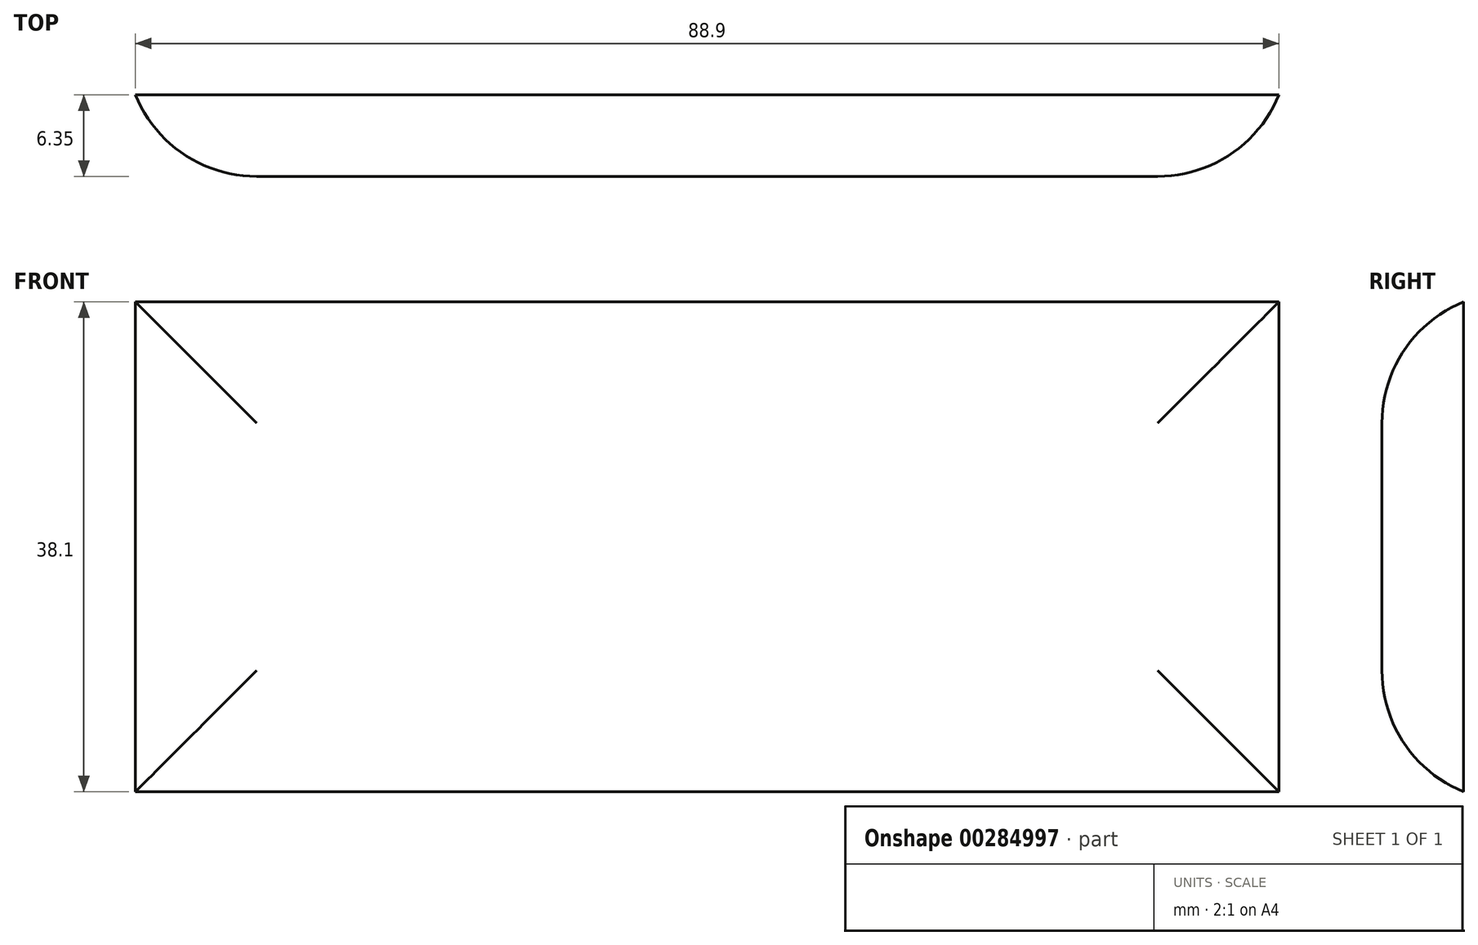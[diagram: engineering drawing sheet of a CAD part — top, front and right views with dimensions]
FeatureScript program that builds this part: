
annotation { "Feature Type Name" : "Feature", "Feature Type Description" : "" }
export const myFeature = defineFeature(function(context is Context, id is Id, definition is map)
    precondition{}
    {
        {
            var Q0;
            Q0=qCreatedBy(makeId("Top.planeOp"),FACE);
            var sketch = newSketch(context, id + "F0", { "sketchPlane" : qUnion([Q0])});
            skLineSegment(sketch, "E0.bottom", {"start": v(-54.1, -12) * mm, "end": v(-143, -12) * mm});
            skLineSegment(sketch, "E0.top", {"start": v(-54.1, -5.66) * mm, "end": v(-143, -5.66) * mm});
            skLineSegment(sketch, "E0.left", {"start": v(-54.1, -12) * mm, "end": v(-54.1, -5.66) * mm});
            skLineSegment(sketch, "E0.right", {"start": v(-143, -12) * mm, "end": v(-143, -5.66) * mm});
            skPoint(sketch, "E0.middle", {"position": v(-98.56, -8.83) * mm});
            skSolve(sketch);
        }
        {
            var Q0;
            Q0=makeQuery(id+"F0.imprint","IMPRINT",FACE,{"disambiguationData":[TD([[makeQuery(id+"F0.imprint","IMPRINT",EDGE,{"derivedFrom":sQuery(id+"F0.wireOp",EDGE,"E0.bottom")}),-1.0]])]});
            extrude(context, id + "F1", {"entities" : qUnion([Q0]), "depth" : 38.1 * mm});
        }
        {
            var Q0;
            Q0=makeQuery(id+"F1.opExtrude","CAP_EDGE",EDGE,{"disambiguationData":[OSD([sQuery(id+"F0.wireOp",EDGE,"E0.bottom")])],"isStart":false});
            var Q1;
            Q1=makeQuery(id+"F1.opExtrude","SWEPT_EDGE",EDGE,{"disambiguationData":[OSD([sQuery(id+"F0.wireOp",EDGE,"E0.bottom"),sQuery(id+"F0.wireOp",EDGE,"E0.left")])]});
            var Q2;
            Q2=makeQuery(id+"F1.opExtrude","CAP_EDGE",EDGE,{"disambiguationData":[OSD([sQuery(id+"F0.wireOp",EDGE,"E0.bottom")])],"isStart":true});
            var Q3;
            Q3=makeQuery(id+"F1.opExtrude","SWEPT_EDGE",EDGE,{"disambiguationData":[OSD([sQuery(id+"F0.wireOp",EDGE,"E0.bottom"),sQuery(id+"F0.wireOp",EDGE,"E0.right")])]});
            fillet(context, id + "F2", {"entities" : qUnion([Q0, Q1, Q2, Q3]), "radius" : 10.16 * mm, "tangentPropagation" : true, "allowEdgeOverflow" : false});
        }
    });
